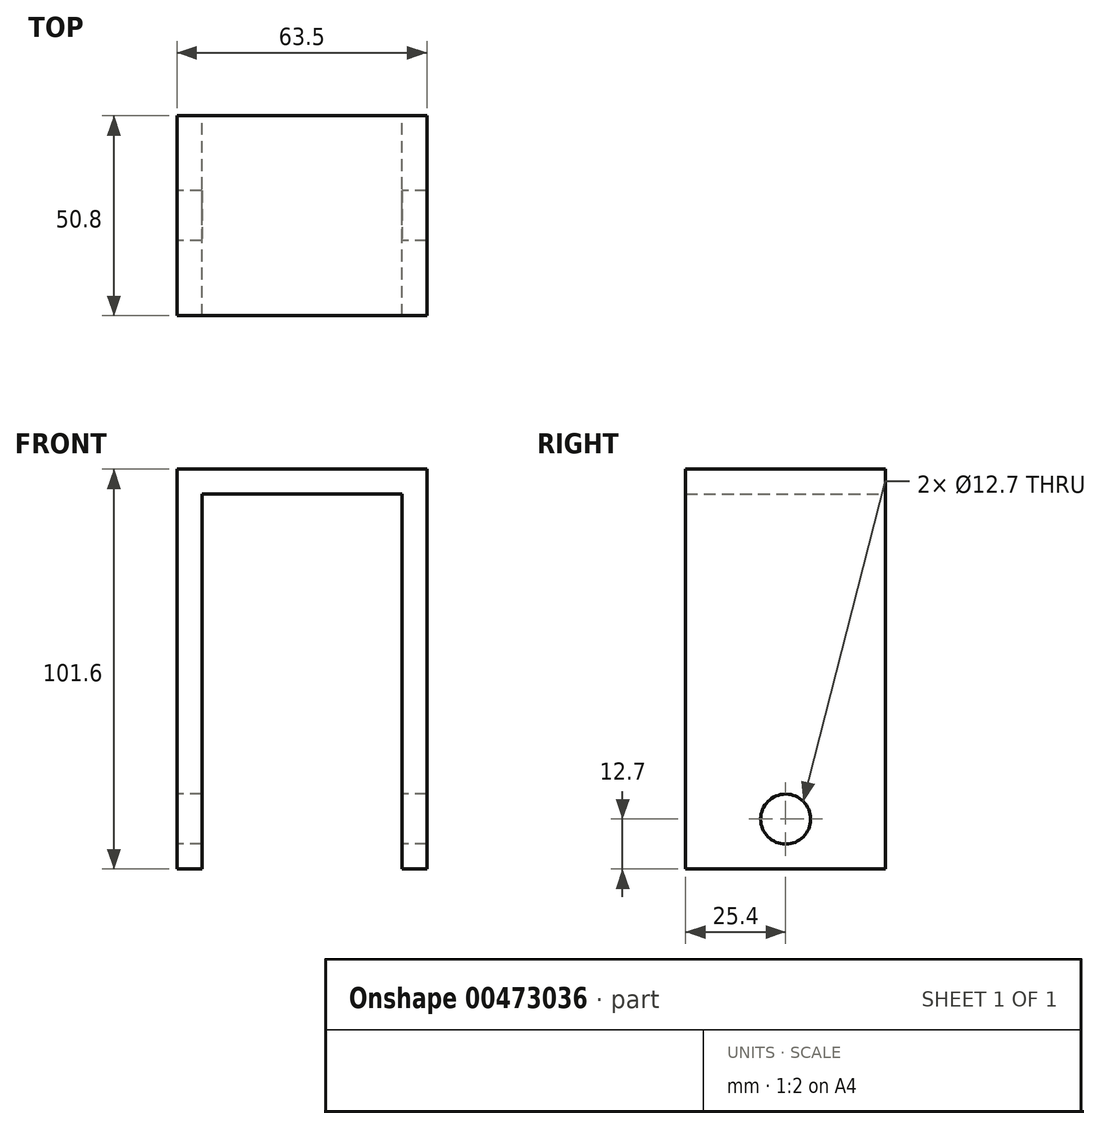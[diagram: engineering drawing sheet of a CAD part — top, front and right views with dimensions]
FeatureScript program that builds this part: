
annotation { "Feature Type Name" : "Feature", "Feature Type Description" : "" }
export const myFeature = defineFeature(function(context is Context, id is Id, definition is map)
    precondition{}
    {
        {
            var Q0;
            Q0=qCreatedBy(makeId("Front.planeOp"),FACE);
            var sketch = newSketch(context, id + "F0", { "sketchPlane" : qUnion([Q0])});
            skLineSegment(sketch, "E0.bottom", {"start": v(0, 0) * mm, "end": v(6.35, 0) * mm});
            skLineSegment(sketch, "E0.top", {"start": v(0, 101.6) * mm, "end": v(63.5, 101.6) * mm});
            skLineSegment(sketch, "E0.left", {"start": v(0, 0) * mm, "end": v(0, 101.6) * mm});
            skLineSegment(sketch, "E0.right", {"start": v(63.5, 0) * mm, "end": v(63.5, 101.6) * mm});
            skLineSegment(sketch, "E1.0", {"start": v(6.35, 0) * mm, "end": v(6.35, 95.25) * mm});
            skLineSegment(sketch, "E2.0", {"start": v(57.15, 0) * mm, "end": v(57.15, 95.25) * mm});
            skLineSegment(sketch, "E3.0", {"start": v(6.35, 95.25) * mm, "end": v(57.15, 95.25) * mm});
            skLineSegment(sketch, "E4.trimOffspring", {"start": v(57.15, 0) * mm, "end": v(63.5, 0) * mm});
            skSolve(sketch);
        }
        {
            var Q0;
            Q0=makeQuery(id+"F0.imprint","IMPRINT",FACE,{"disambiguationData":[TD([[makeQuery(id+"F0.imprint","IMPRINT",EDGE,{"derivedFrom":sQuery(id+"F0.wireOp",EDGE,"E0.bottom")}),1.0]])]});
            extrude(context, id + "F1", {"entities" : qUnion([Q0]), "depth" : 50.8 * mm});
        }
        {
            var Q0;
            Q0=makeQuery(id+"F1.opExtrude","SWEPT_FACE",FACE,{"disambiguationData":[OSD([sQuery(id+"F0.wireOp",EDGE,"E0.left")])]});
            var sketch = newSketch(context, id + "F2", { "sketchPlane" : qUnion([Q0])});
            skCircle(sketch, "E5", {"center": v(25.4, 12.7) * mm, "radius": 6.35 * mm});
            skSolve(sketch);
        }
        {
            var Q0;
            Q0=makeQuery(id+"F2.imprint","IMPRINT",FACE,{"disambiguationData":[TD([[makeQuery(id+"F2.imprint","IMPRINT",EDGE,{"derivedFrom":sQuery(id+"F2.wireOp",EDGE,"E5")}),1.0]])]});
            extrude(context, id + "F3", {"entities" : qUnion([Q0]), "operationType" : NewBodyOperationType.REMOVE, "endBound" : BoundingType.THROUGH_ALL, "oppositeDirection" : true, "depth" : 76.2 * mm});
        }
    });
